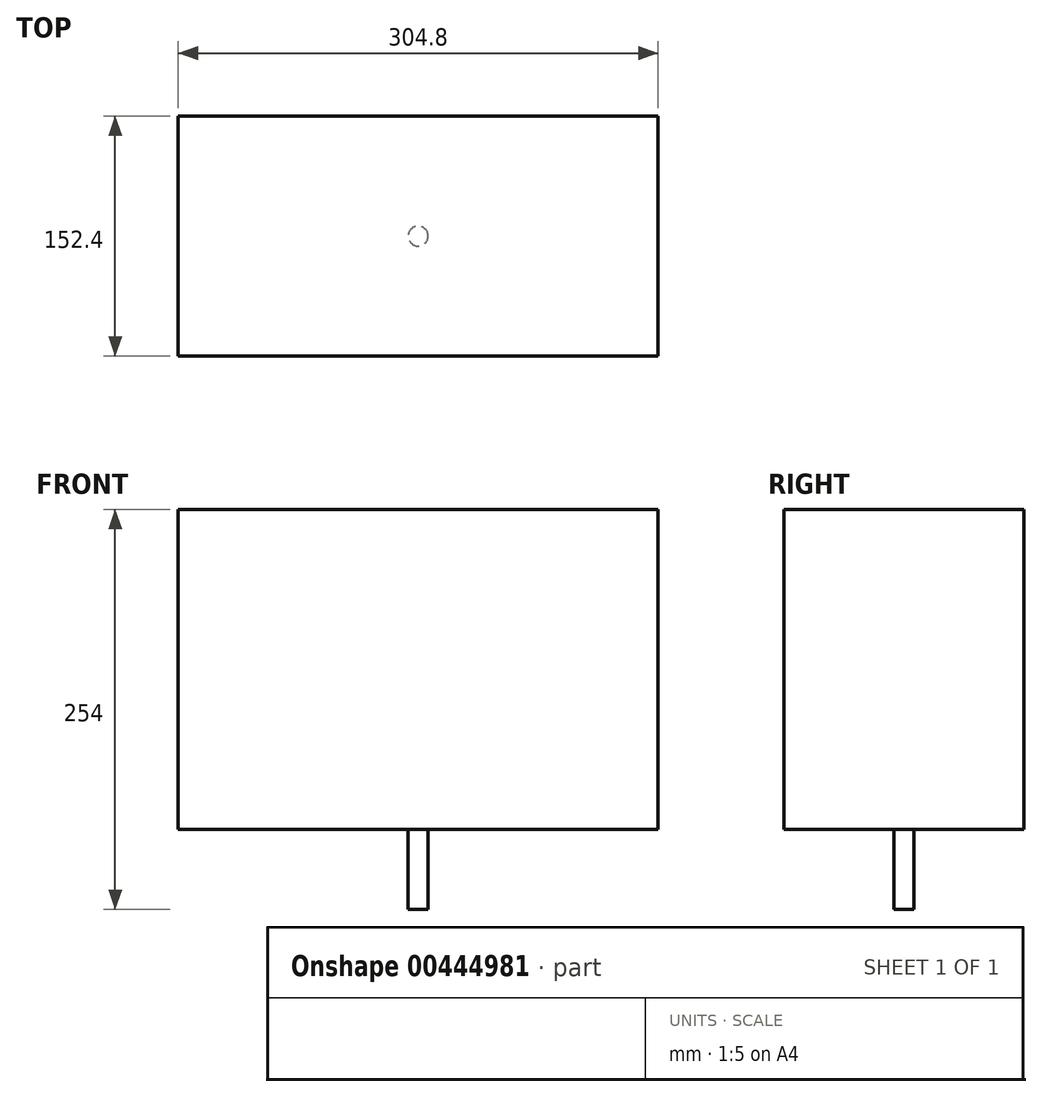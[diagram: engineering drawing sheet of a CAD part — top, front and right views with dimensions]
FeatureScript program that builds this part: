
annotation { "Feature Type Name" : "Feature", "Feature Type Description" : "" }
export const myFeature = defineFeature(function(context is Context, id is Id, definition is map)
    precondition{}
    {
        {
            var Q0;
            Q0=qCreatedBy(makeId("Front.planeOp"),FACE);
            var sketch = newSketch(context, id + "F0", { "sketchPlane" : qUnion([Q0])});
            skLineSegment(sketch, "E0.bottom", {"start": v(-152.4, 203.2) * mm, "end": v(152.4, 203.2) * mm});
            skLineSegment(sketch, "E0.top", {"start": v(-152.4, 0) * mm, "end": v(152.4, 0) * mm});
            skLineSegment(sketch, "E0.left", {"start": v(-152.4, 203.2) * mm, "end": v(-152.4, 0) * mm});
            skLineSegment(sketch, "E0.right", {"start": v(152.4, 203.2) * mm, "end": v(152.4, 0) * mm});
            skLineSegment(sketch, "E1", {"start": v(0, 203.2) * mm, "end": v(0, 0) * mm});
            skSolve(sketch);
        }
        {
            var Q0;
            Q0 = qSketchRegion(id + "F0", true);
            extrude(context, id + "F1", {"entities" : qUnion([Q0]), "depth" : 152.4 * mm});
        }
        {
            var Q0;
            Q0=makeQuery(id+"F1.opExtrude","SWEPT_FACE",FACE,{"disambiguationData":[OSD([sQuery(id+"F0.wireOp",EDGE,"E0.top")])]});
            var sketch = newSketch(context, id + "F2", { "sketchPlane" : qUnion([Q0])});
            skCircle(sketch, "E2", {"center": v(0, 76.2) * mm, "radius": 6.35 * mm});
            skSolve(sketch);
        }
        {
            var Q0;
            Q0 = qSketchRegion(id + "F2", true);
            extrude(context, id + "F3", {"entities" : qUnion([Q0]), "operationType" : NewBodyOperationType.ADD, "depth" : 50.8 * mm});
        }
    });
